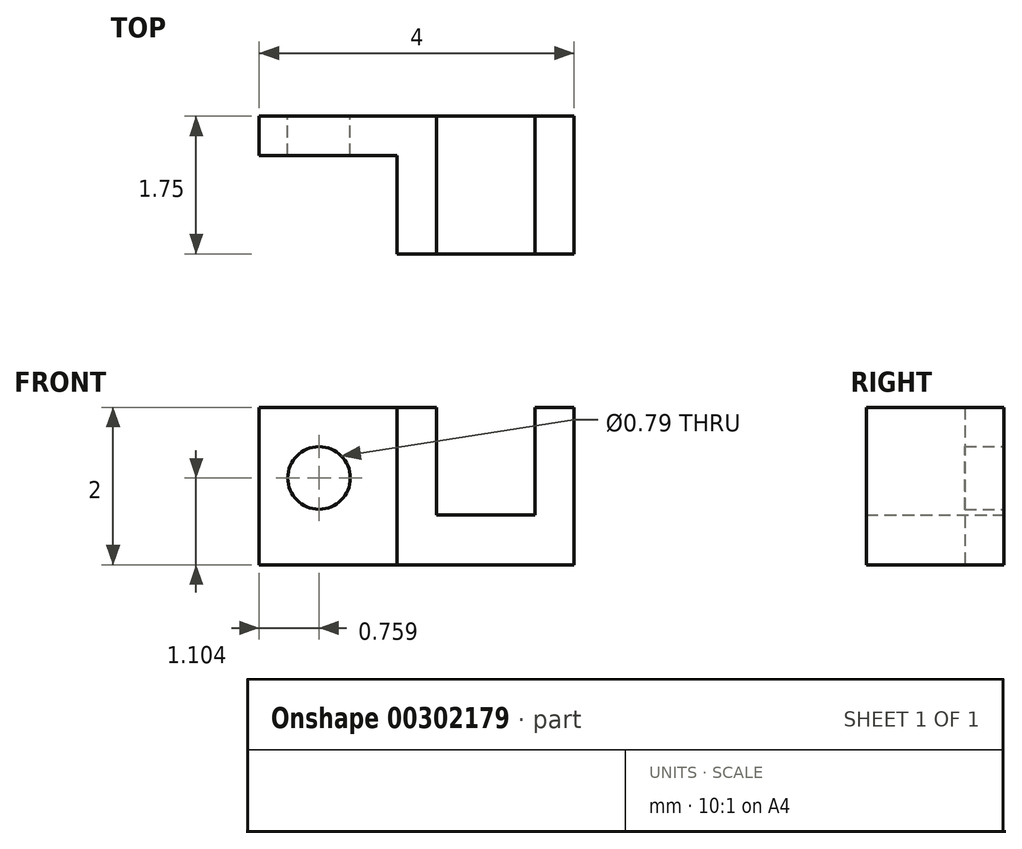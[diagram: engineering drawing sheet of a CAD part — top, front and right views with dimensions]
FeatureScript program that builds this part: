
annotation { "Feature Type Name" : "Feature", "Feature Type Description" : "" }
export const myFeature = defineFeature(function(context is Context, id is Id, definition is map)
    precondition{}
    {
        {
            var Q0;
            Q0=qCreatedBy(makeId("Front.planeOp"),FACE);
            var sketch = newSketch(context, id + "F0", { "sketchPlane" : qUnion([Q0])});
            skLineSegment(sketch, "E0.bottom", {"start": v(-25.5, -33.13) * mm, "end": v(-23.74, -33.13) * mm});
            skLineSegment(sketch, "E0.top", {"start": v(-25.5, -35.13) * mm, "end": v(-23.74, -35.13) * mm});
            skLineSegment(sketch, "E0.left", {"start": v(-25.5, -33.13) * mm, "end": v(-25.5, -35.13) * mm});
            skLineSegment(sketch, "E0.right", {"start": v(-23.74, -33.13) * mm, "end": v(-23.74, -35.13) * mm});
            skLineSegment(sketch, "E1.bottom", {"start": v(-23.74, -33.13) * mm, "end": v(-23.24, -33.13) * mm});
            skLineSegment(sketch, "E1.top", {"start": v(-23.74, -35.13) * mm, "end": v(-21.5, -35.13) * mm});
            skLineSegment(sketch, "E1.right", {"start": v(-21.5, -33.13) * mm, "end": v(-21.5, -35.13) * mm});
            skLineSegment(sketch, "E2", {"start": v(-21.5, -33.13) * mm, "end": v(-22, -33.13) * mm});
            skLineSegment(sketch, "E3.top", {"start": v(-23.24, -34.5) * mm, "end": v(-22, -34.5) * mm});
            skLineSegment(sketch, "E3.left", {"start": v(-23.24, -33.13) * mm, "end": v(-23.24, -34.5) * mm});
            skLineSegment(sketch, "E3.right", {"start": v(-22, -33.13) * mm, "end": v(-22, -34.5) * mm});
            skLineSegment(sketch, "E4.trimOffspring", {"start": v(-22, -33.13) * mm, "end": v(-21.5, -33.13) * mm});
            skCircle(sketch, "E5", {"center": v(-24.73, -34.03) * mm, "radius": 0.4 * mm});
            skSolve(sketch);
        }
        {
            var Q0;
            {var subQ2=sQuery(id+"F0.wireOp",EDGE,"E1.top");Q0=makeQuery(id+"F0.imprint","IMPRINT",FACE,{"disambiguationData":[TD([[makeQuery(id+"F0.imprint","IMPRINT",EDGE,{"derivedFrom":subQ2}),1.0]])]});}
            extrude(context, id + "F1", {"entities" : qUnion([Q0]), "depth" : 1.75 * mm});
        }
        {
            var Q0;
            {var subQ1=sQuery(id+"F0.wireOp",EDGE,"E0.bottom");Q0=makeQuery(id+"F0.imprint","IMPRINT",FACE,{"disambiguationData":[TD([[makeQuery(id+"F0.imprint","IMPRINT",EDGE,{"derivedFrom":subQ1}),-1.0]])]});}
            extrude(context, id + "F2", {"entities" : qUnion([Q0]), "operationType" : NewBodyOperationType.ADD, "depth" : .5 * mm});
        }
    });
